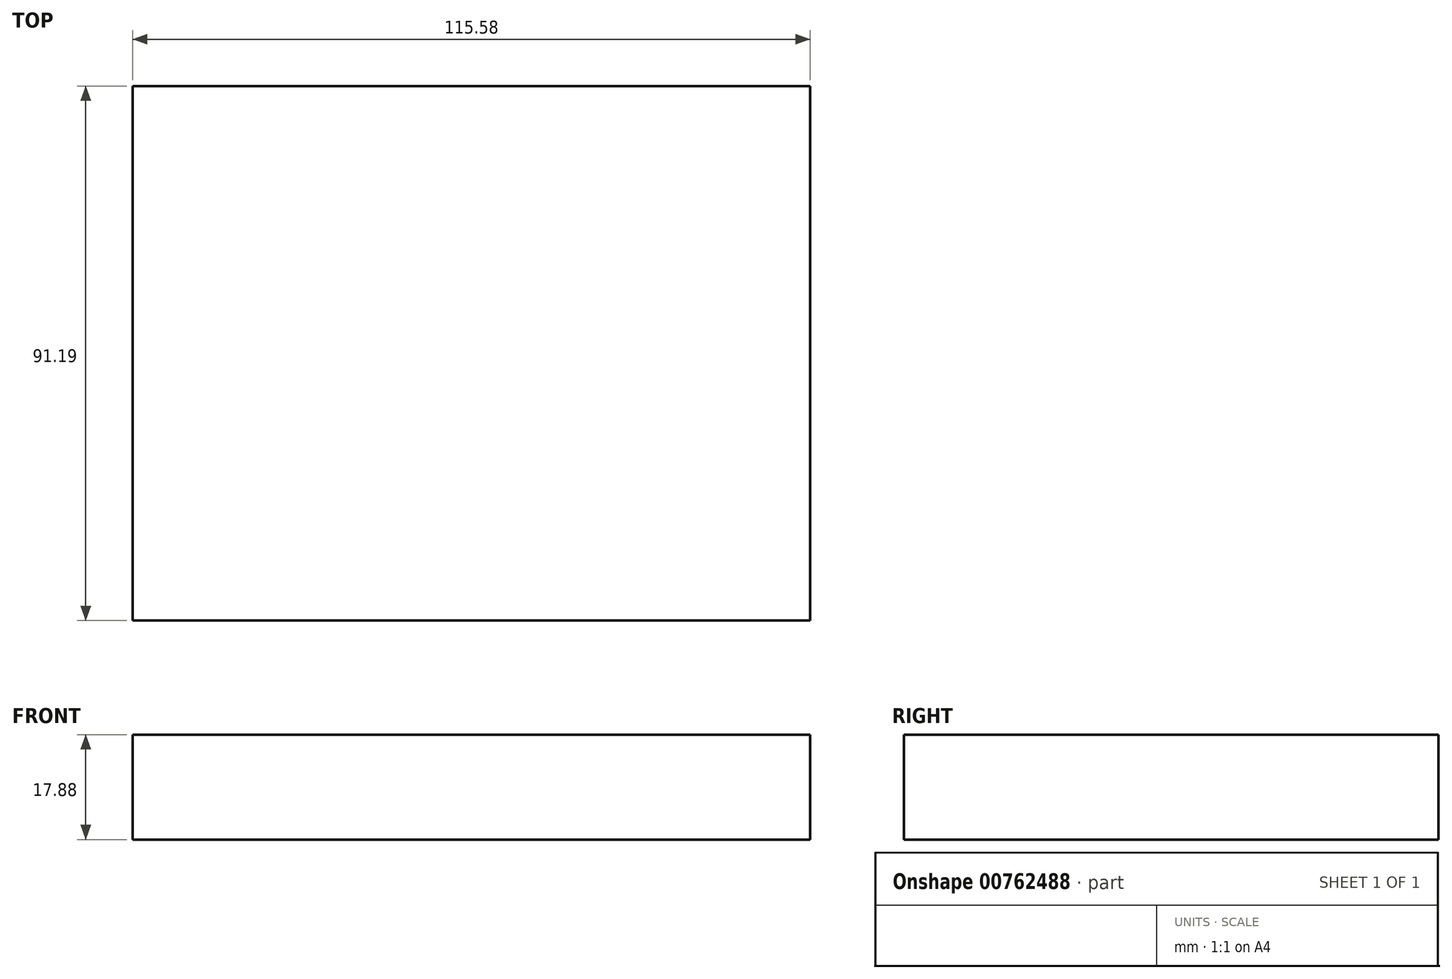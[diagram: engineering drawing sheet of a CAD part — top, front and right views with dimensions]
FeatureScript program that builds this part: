
annotation { "Feature Type Name" : "Feature", "Feature Type Description" : "" }
export const myFeature = defineFeature(function(context is Context, id is Id, definition is map)
    precondition{}
    {
        {
            var Q0;
            Q0=qCreatedBy(makeId("Front.planeOp"),FACE);
            var sketch = newSketch(context, id + "F0", { "sketchPlane" : qUnion([Q0])});
            skLineSegment(sketch, "E0.bottom", {"start": v(-62.42, 5.42) * mm, "end": v(53.16, 5.42) * mm});
            skLineSegment(sketch, "E0.top", {"start": v(-62.42, -12.46) * mm, "end": v(53.16, -12.46) * mm});
            skLineSegment(sketch, "E0.left", {"start": v(-62.42, 5.42) * mm, "end": v(-62.42, -12.46) * mm});
            skLineSegment(sketch, "E0.right", {"start": v(53.16, 5.42) * mm, "end": v(53.16, -12.46) * mm});
            skSolve(sketch);
        }
        {
            var Q0;
            Q0=makeQuery(id+"F0.imprint","IMPRINT",FACE,{"disambiguationData":[TD([[makeQuery(id+"F0.imprint","IMPRINT",EDGE,{"derivedFrom":sQuery(id+"F0.wireOp",EDGE,"E0.bottom")}),-1.0]])]});
            extrude(context, id + "F1", {"entities" : qUnion([Q0]), "depth" : 91.19 * mm, "offsetDistance" : 25.4 * mm});
        }
    });
